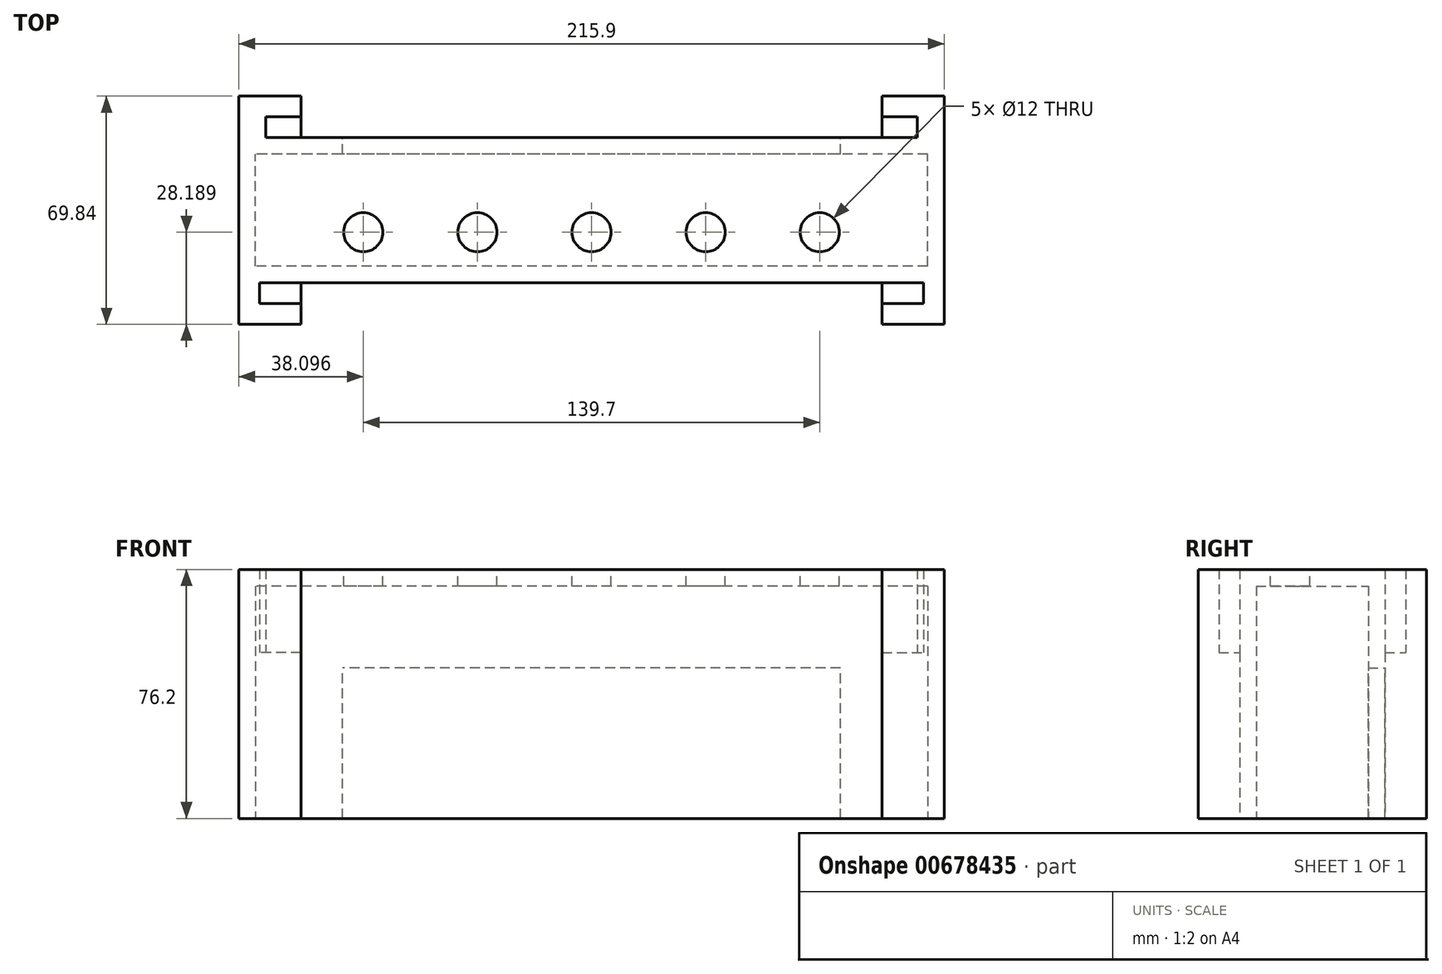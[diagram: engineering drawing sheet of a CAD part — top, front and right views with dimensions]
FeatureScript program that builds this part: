
annotation { "Feature Type Name" : "Feature", "Feature Type Description" : "" }
export const myFeature = defineFeature(function(context is Context, id is Id, definition is map)
    precondition{}
    {
        {
            var Q0;
            Q0=qCreatedBy(makeId("Top.planeOp"),FACE);
            var sketch = newSketch(context, id + "F0", { "sketchPlane" : qUnion([Q0])});
            skLineSegment(sketch, "E0.bottom", {"start": v(105.18, -22.23) * mm, "end": v(-110.72, -22.23) * mm});
            skLineSegment(sketch, "E0.top", {"start": v(105.18, 22.23) * mm, "end": v(-110.72, 22.22) * mm});
            skLineSegment(sketch, "E0.left", {"start": v(105.18, -22.23) * mm, "end": v(105.18, 22.22) * mm});
            skLineSegment(sketch, "E0.right", {"start": v(-110.72, -22.23) * mm, "end": v(-110.72, 22.22) * mm});
            skPoint(sketch, "E0.middle", {"position": v(-2.77, 0) * mm});
            skSolve(sketch);
        }
        {
            var Q0;
            Q0=makeQuery(id+"F0.imprint","IMPRINT",FACE,{"disambiguationData":[TD([[makeQuery(id+"F0.imprint","IMPRINT",EDGE,{"derivedFrom":sQuery(id+"F0.wireOp",EDGE,"E0.bottom")}),-1.0]])]});
            extrude(context, id + "F1", {"entities" : qUnion([Q0]), "depth" : 76.2 * mm, "offsetDistance" : 25.4 * mm});
        }
        {
            var Q0;
            Q0=makeQuery(id+"F1.opExtrude","CAP_FACE",FACE,{"disambiguationData":[OSD([sQuery(id+"F0.wireOp",EDGE,"E0.bottom"),sQuery(id+"F0.wireOp",EDGE,"E0.top"),sQuery(id+"F0.wireOp",EDGE,"E0.left"),sQuery(id+"F0.wireOp",EDGE,"E0.right")])],"isStart":true});
            shell(context, id + "F2", {"entities" : qUnion([Q0]), "thickness" : 5.08 * mm});
        }
        {
            var Q0;
            Q0=makeQuery(id+"F1.opExtrude","SWEPT_FACE",FACE,{"disambiguationData":[OSD([sQuery(id+"F0.wireOp",EDGE,"E0.bottom")])]});
            var sketch = newSketch(context, id + "F3", { "sketchPlane" : qUnion([Q0])});
            skLineSegment(sketch, "E1.bottom", {"start": v(-110.72, 76.2) * mm, "end": v(-104.37, 76.2) * mm});
            skLineSegment(sketch, "E1.top", {"start": v(-110.72, 0) * mm, "end": v(-104.37, 0) * mm});
            skLineSegment(sketch, "E1.left", {"start": v(-110.72, 76.2) * mm, "end": v(-110.72, 0) * mm});
            skLineSegment(sketch, "E1.right", {"start": v(-104.37, 76.2) * mm, "end": v(-104.37, 0) * mm});
            skLineSegment(sketch, "E2.bottom", {"start": v(105.18, 76.2) * mm, "end": v(98.83, 76.2) * mm});
            skLineSegment(sketch, "E2.top", {"start": v(105.18, 0) * mm, "end": v(98.83, 0) * mm});
            skLineSegment(sketch, "E2.left", {"start": v(105.18, 76.2) * mm, "end": v(105.18, 0) * mm});
            skLineSegment(sketch, "E2.right", {"start": v(98.83, 76.2) * mm, "end": v(98.83, 0) * mm});
            skSolve(sketch);
        }
        {
            var Q0;
            Q0=makeQuery(id+"F1.opExtrude","SWEPT_FACE",FACE,{"disambiguationData":[OSD([sQuery(id+"F0.wireOp",EDGE,"E0.top")])]});
            var sketch = newSketch(context, id + "F4", { "sketchPlane" : qUnion([Q0])});
            skLineSegment(sketch, "E3.bottom", {"start": v(-105.18, 76.2) * mm, "end": v(-98.83, 76.2) * mm});
            skLineSegment(sketch, "E3.top", {"start": v(-105.18, 0) * mm, "end": v(-98.83, 0) * mm});
            skLineSegment(sketch, "E3.left", {"start": v(-105.18, 76.2) * mm, "end": v(-105.18, 0) * mm});
            skLineSegment(sketch, "E3.right", {"start": v(-98.83, 76.2) * mm, "end": v(-98.83, 0) * mm});
            skLineSegment(sketch, "E4.bottom", {"start": v(110.72, 76.2) * mm, "end": v(104.37, 76.2) * mm});
            skLineSegment(sketch, "E4.top", {"start": v(110.72, 0) * mm, "end": v(104.37, 0) * mm});
            skLineSegment(sketch, "E4.left", {"start": v(110.72, 76.2) * mm, "end": v(110.72, 0) * mm});
            skLineSegment(sketch, "E4.right", {"start": v(104.37, 76.2) * mm, "end": v(104.37, 0) * mm});
            skSolve(sketch);
        }
        {
            var Q0;
            Q0=makeQuery(id+"F3.imprint","IMPRINT",FACE,{"disambiguationData":[TD([[makeQuery(id+"F3.imprint","IMPRINT",EDGE,{"derivedFrom":sQuery(id+"F3.wireOp",EDGE,"E1.bottom")}),1.0]])]});
            var Q1;
            Q1=makeQuery(id+"F3.imprint","IMPRINT",FACE,{"disambiguationData":[TD([[makeQuery(id+"F3.imprint","IMPRINT",EDGE,{"derivedFrom":sQuery(id+"F3.wireOp",EDGE,"E2.bottom")}),1.0]])]});
            extrude(context, id + "F5", {"entities" : qUnion([Q0, Q1]), "operationType" : NewBodyOperationType.ADD, "depth" : 12.7 * mm, "offsetDistance" : 25.4 * mm});
        }
        {
            var Q0;
            Q0=makeQuery(id+"F4.imprint","IMPRINT",FACE,{"disambiguationData":[TD([[makeQuery(id+"F4.imprint","IMPRINT",EDGE,{"derivedFrom":sQuery(id+"F4.wireOp",EDGE,"E3.bottom")}),-1.0]])]});
            var Q1;
            Q1=makeQuery(id+"F4.imprint","IMPRINT",FACE,{"disambiguationData":[TD([[makeQuery(id+"F4.imprint","IMPRINT",EDGE,{"derivedFrom":sQuery(id+"F4.wireOp",EDGE,"E4.bottom")}),-1.0]])]});
            extrude(context, id + "F6", {"entities" : qUnion([Q0, Q1]), "operationType" : NewBodyOperationType.ADD, "depth" : 12.7 * mm, "offsetDistance" : 25.4 * mm});
        }
        {
            var Q0;
            Q0=makeQuery(id+"FRrmfCGgLjqdVNs_1.boolean.opBoolean","MERGE",FACE,{"derivedFrom":[makeQuery(id+"FzGourxVZPiTFxx_1.boolean.opBoolean","MERGE",FACE,{"derivedFrom":[makeQuery(id+"F6.boolean.opBoolean","MERGE",FACE,{"derivedFrom":[makeQuery(id+"F5.boolean.opBoolean","MERGE",FACE,{"derivedFrom":[makeQuery(id+"F1.opExtrude","CAP_FACE",FACE,{"disambiguationData":[OSD([sQuery(id+"F0.wireOp",EDGE,"E0.bottom"),sQuery(id+"F0.wireOp",EDGE,"E0.top"),sQuery(id+"F0.wireOp",EDGE,"E0.left"),sQuery(id+"F0.wireOp",EDGE,"E0.right")])],"isStart":false}),makeQuery(id+"F5.opExtrude","SWEPT_FACE",FACE,{"disambiguationData":[OSD([sQuery(id+"F3.wireOp",EDGE,"E1.bottom")])]}),makeQuery(id+"F5.opExtrude","SWEPT_FACE",FACE,{"disambiguationData":[OSD([sQuery(id+"F3.wireOp",EDGE,"E2.bottom")])]})]}),makeQuery(id+"F6.opExtrude","SWEPT_FACE",FACE,{"disambiguationData":[OSD([sQuery(id+"F4.wireOp",EDGE,"E3.bottom")])]}),makeQuery(id+"F6.opExtrude","SWEPT_FACE",FACE,{"disambiguationData":[OSD([sQuery(id+"F4.wireOp",EDGE,"E4.bottom")])]})]}),makeQuery(id+"FzGourxVZPiTFxx_1.opExtrude","SWEPT_FACE",FACE,{"disambiguationData":[OSD([sQuery(id+"FrnQMVu3a4CgWtk_1.wireOp",EDGE,"r2tbibCh-ezkN-9FMi-7AQF-PA2gdZFEVCPD.bottom")])]}),makeQuery(id+"FzGourxVZPiTFxx_1.opExtrude","SWEPT_FACE",FACE,{"disambiguationData":[OSD([sQuery(id+"FhxCwb5BdVCvZEk_1.wireOp",EDGE,"8bSKoqo4-8QkT-eqxh-rGB9-fyDsR7UwIenD.bottom")])]})]}),makeQuery(id+"FRrmfCGgLjqdVNs_1.opExtrude","SWEPT_FACE",FACE,{"disambiguationData":[OSD([sQuery(id+"FhhxslobYrObnGy_1.wireOp",EDGE,"or8zbcxm-MRwS-TR7M-PYDy-Oy9PLmHRumrI.bottom")])]}),makeQuery(id+"FRrmfCGgLjqdVNs_1.opExtrude","SWEPT_FACE",FACE,{"disambiguationData":[OSD([sQuery(id+"FWsOcmM0LLO9Jgi_1.wireOp",EDGE,"o5xxpl94-z1vP-JHRe-kS0J-yNKfIfnKd3mt.bottom")])]})]});
            var sketch = newSketch(context, id + "F7", { "sketchPlane" : qUnion([Q0])});
            skCircle(sketch, "E5", {"center": v(67.08, -6.73) * mm, "radius": 6 * mm});
            skCircle(sketch, "E6", {"center": v(32.15, -6.73) * mm, "radius": 6 * mm});
            skCircle(sketch, "E7", {"center": v(-2.77, -6.73) * mm, "radius": 6 * mm});
            skCircle(sketch, "E8", {"center": v(-37.7, -6.73) * mm, "radius": 6 * mm});
            skCircle(sketch, "E9", {"center": v(-72.62, -6.73) * mm, "radius": 6 * mm});
            skSolve(sketch);
        }
        {
            var Q0;
            Q0=makeQuery(id+"F6.opExtrude","SWEPT_FACE",FACE,{"disambiguationData":[OSD([sQuery(id+"F4.wireOp",EDGE,"E3.right")])]});
            var sketch = newSketch(context, id + "F8", { "sketchPlane" : qUnion([Q0])});
            skLineSegment(sketch, "E10.bottom", {"start": v(-34.93, 76.2) * mm, "end": v(-28.58, 76.2) * mm});
            skLineSegment(sketch, "E10.top", {"start": v(-34.93, 0) * mm, "end": v(-28.58, 0) * mm});
            skLineSegment(sketch, "E10.left", {"start": v(-34.93, 76.2) * mm, "end": v(-34.93, 0) * mm});
            skLineSegment(sketch, "E10.right", {"start": v(-28.58, 76.2) * mm, "end": v(-28.58, 0) * mm});
            skLineSegment(sketch, "E11.bottom", {"start": v(-28.58, 0) * mm, "end": v(-22.23, 0) * mm});
            skLineSegment(sketch, "E11.top", {"start": v(-28.58, 50.8) * mm, "end": v(-22.23, 50.8) * mm});
            skLineSegment(sketch, "E11.left", {"start": v(-28.58, 0) * mm, "end": v(-28.58, 50.8) * mm});
            skLineSegment(sketch, "E11.right", {"start": v(-22.23, 0) * mm, "end": v(-22.23, 50.8) * mm});
            skSolve(sketch);
        }
        {
            var Q0;
            Q0=makeQuery(id+"F8.imprint","IMPRINT",FACE,{"disambiguationData":[TD([[makeQuery(id+"F8.imprint","IMPRINT",EDGE,{"derivedFrom":sQuery(id+"F8.wireOp",EDGE,"E10.bottom")}),-1.0]])]});
            var Q1;
            Q1=makeQuery(id+"F8.imprint","IMPRINT",FACE,{"disambiguationData":[TD([[makeQuery(id+"F8.imprint","IMPRINT",EDGE,{"derivedFrom":sQuery(id+"F8.wireOp",EDGE,"E11.bottom")}),1.0]])]});
            extrude(context, id + "F9", {"entities" : qUnion([Q0, Q1]), "operationType" : NewBodyOperationType.ADD, "depth" : 12.7 * mm, "offsetDistance" : 25.4 * mm});
        }
        {
            var Q0;
            Q0=makeQuery(id+"F6.opExtrude","SWEPT_FACE",FACE,{"disambiguationData":[OSD([sQuery(id+"F4.wireOp",EDGE,"E4.right")])]});
            var sketch = newSketch(context, id + "F10", { "sketchPlane" : qUnion([Q0])});
            skLineSegment(sketch, "E12.bottom", {"start": v(34.93, 76.2) * mm, "end": v(28.58, 76.2) * mm});
            skLineSegment(sketch, "E12.top", {"start": v(34.93, 0) * mm, "end": v(28.58, 0) * mm});
            skLineSegment(sketch, "E12.left", {"start": v(34.93, 76.2) * mm, "end": v(34.93, 0) * mm});
            skLineSegment(sketch, "E12.right", {"start": v(28.58, 76.2) * mm, "end": v(28.58, 0) * mm});
            skLineSegment(sketch, "E13.bottom", {"start": v(28.58, 0) * mm, "end": v(22.23, 0) * mm});
            skLineSegment(sketch, "E13.top", {"start": v(28.58, 50.8) * mm, "end": v(22.23, 50.8) * mm});
            skLineSegment(sketch, "E13.left", {"start": v(28.58, 0) * mm, "end": v(28.58, 50.8) * mm});
            skLineSegment(sketch, "E13.right", {"start": v(22.23, 0) * mm, "end": v(22.23, 50.8) * mm});
            skSolve(sketch);
        }
        {
            var Q0;
            Q0=makeQuery(id+"F10.imprint","IMPRINT",FACE,{"disambiguationData":[TD([[makeQuery(id+"F10.imprint","IMPRINT",EDGE,{"derivedFrom":sQuery(id+"F10.wireOp",EDGE,"E12.bottom")}),1.0]])]});
            var Q1;
            Q1=makeQuery(id+"F10.imprint","IMPRINT",FACE,{"disambiguationData":[TD([[makeQuery(id+"F10.imprint","IMPRINT",EDGE,{"derivedFrom":sQuery(id+"F10.wireOp",EDGE,"E13.bottom")}),-1.0]])]});
            extrude(context, id + "F11", {"entities" : qUnion([Q0, Q1]), "operationType" : NewBodyOperationType.ADD, "depth" : 12.7 * mm, "offsetDistance" : 25.4 * mm});
        }
        {
            var Q0;
            Q0=makeQuery(id+"F5.opExtrude","SWEPT_FACE",FACE,{"disambiguationData":[OSD([sQuery(id+"F3.wireOp",EDGE,"E1.right")])]});
            var sketch = newSketch(context, id + "F12", { "sketchPlane" : qUnion([Q0])});
            skLineSegment(sketch, "E14.bottom", {"start": v(-34.93, 0) * mm, "end": v(-28.58, 0) * mm});
            skLineSegment(sketch, "E14.top", {"start": v(-34.93, 76.2) * mm, "end": v(-28.58, 76.2) * mm});
            skLineSegment(sketch, "E14.left", {"start": v(-34.93, 0) * mm, "end": v(-34.93, 76.2) * mm});
            skLineSegment(sketch, "E14.right", {"start": v(-28.58, 0) * mm, "end": v(-28.58, 76.2) * mm});
            skLineSegment(sketch, "E15.bottom", {"start": v(-28.58, 0) * mm, "end": v(-22.23, 0) * mm});
            skLineSegment(sketch, "E15.top", {"start": v(-28.58, 50.8) * mm, "end": v(-22.23, 50.8) * mm});
            skLineSegment(sketch, "E15.left", {"start": v(-28.58, 0) * mm, "end": v(-28.58, 50.8) * mm});
            skLineSegment(sketch, "E15.right", {"start": v(-22.23, 0) * mm, "end": v(-22.23, 50.8) * mm});
            skSolve(sketch);
        }
        {
            var Q0;
            Q0=makeQuery(id+"F12.imprint","IMPRINT",FACE,{"disambiguationData":[TD([[makeQuery(id+"F12.imprint","IMPRINT",EDGE,{"derivedFrom":sQuery(id+"F12.wireOp",EDGE,"E14.bottom")}),1.0]])]});
            var Q1;
            Q1=makeQuery(id+"F12.imprint","IMPRINT",FACE,{"disambiguationData":[TD([[makeQuery(id+"F12.imprint","IMPRINT",EDGE,{"derivedFrom":sQuery(id+"F12.wireOp",EDGE,"E15.bottom")}),1.0]])]});
            extrude(context, id + "F13", {"entities" : qUnion([Q0, Q1]), "operationType" : NewBodyOperationType.ADD, "depth" : 12.7 * mm, "offsetDistance" : 25.4 * mm});
        }
        {
            var Q0;
            Q0=makeQuery(id+"F5.opExtrude","SWEPT_FACE",FACE,{"disambiguationData":[OSD([sQuery(id+"F3.wireOp",EDGE,"E2.right")])]});
            var sketch = newSketch(context, id + "F14", { "sketchPlane" : qUnion([Q0])});
            skLineSegment(sketch, "E16.bottom", {"start": v(34.93, 76.2) * mm, "end": v(28.58, 76.2) * mm});
            skLineSegment(sketch, "E16.top", {"start": v(34.93, 0) * mm, "end": v(28.58, 0) * mm});
            skLineSegment(sketch, "E16.left", {"start": v(34.93, 76.2) * mm, "end": v(34.93, 0) * mm});
            skLineSegment(sketch, "E16.right", {"start": v(28.58, 76.2) * mm, "end": v(28.58, 0) * mm});
            skLineSegment(sketch, "E17.bottom", {"start": v(28.58, 0) * mm, "end": v(22.23, 0) * mm});
            skLineSegment(sketch, "E17.top", {"start": v(28.58, 50.8) * mm, "end": v(22.23, 50.8) * mm});
            skLineSegment(sketch, "E17.left", {"start": v(28.58, 0) * mm, "end": v(28.58, 50.8) * mm});
            skLineSegment(sketch, "E17.right", {"start": v(22.23, 0) * mm, "end": v(22.23, 50.8) * mm});
            skSolve(sketch);
        }
        {
            var Q0;
            Q0=makeQuery(id+"F14.imprint","IMPRINT",FACE,{"disambiguationData":[TD([[makeQuery(id+"F14.imprint","IMPRINT",EDGE,{"derivedFrom":sQuery(id+"F14.wireOp",EDGE,"E16.bottom")}),1.0]])]});
            var Q1;
            Q1=makeQuery(id+"F14.imprint","IMPRINT",FACE,{"disambiguationData":[TD([[makeQuery(id+"F14.imprint","IMPRINT",EDGE,{"derivedFrom":sQuery(id+"F14.wireOp",EDGE,"E17.bottom")}),-1.0]])]});
            extrude(context, id + "F15", {"entities" : qUnion([Q0, Q1]), "operationType" : NewBodyOperationType.ADD, "depth" : 12.7 * mm, "offsetDistance" : 25.4 * mm});
        }
        {
            var Q0;
            Q0=makeQuery(id+"F1.opExtrude","SWEPT_FACE",FACE,{"disambiguationData":[OSD([sQuery(id+"F0.wireOp",EDGE,"E0.top")])]});
            var sketch = newSketch(context, id + "F16", { "sketchPlane" : qUnion([Q0])});
            skLineSegment(sketch, "E18.bottom", {"start": v(-73.43, 0) * mm, "end": v(78.97, 0) * mm});
            skLineSegment(sketch, "E18.top", {"start": v(-73.43, 46.08) * mm, "end": v(78.97, 46.08) * mm});
            skLineSegment(sketch, "E18.left", {"start": v(-73.43, 0) * mm, "end": v(-73.43, 46.08) * mm});
            skLineSegment(sketch, "E18.right", {"start": v(78.97, 0) * mm, "end": v(78.97, 46.08) * mm});
            skSolve(sketch);
        }
        {
            var Q0;
            Q0=makeQuery(id+"F16.imprint","IMPRINT",FACE,{"disambiguationData":[TD([[makeQuery(id+"F16.imprint","IMPRINT",EDGE,{"derivedFrom":sQuery(id+"F16.wireOp",EDGE,"E18.bottom")}),1.0]])]});
            extrude(context, id + "F17", {"entities" : qUnion([Q0]), "operationType" : NewBodyOperationType.REMOVE, "oppositeDirection" : true, "depth" : 5.08 * mm, "offsetDistance" : 25.4 * mm});
        }
        {
            var Q0;
            Q0=makeQuery(id+"F7.imprint","IMPRINT",FACE,{"disambiguationData":[TD([[makeQuery(id+"F7.imprint","IMPRINT",EDGE,{"derivedFrom":sQuery(id+"F7.wireOp",EDGE,"E5")}),1.0]])]});
            var Q1;
            Q1=makeQuery(id+"F7.imprint","IMPRINT",FACE,{"disambiguationData":[TD([[makeQuery(id+"F7.imprint","IMPRINT",EDGE,{"derivedFrom":sQuery(id+"F7.wireOp",EDGE,"E6")}),1.0]])]});
            var Q2;
            Q2=makeQuery(id+"F7.imprint","IMPRINT",FACE,{"disambiguationData":[TD([[makeQuery(id+"F7.imprint","IMPRINT",EDGE,{"derivedFrom":sQuery(id+"F7.wireOp",EDGE,"E7")}),1.0]])]});
            var Q3;
            Q3=makeQuery(id+"F7.imprint","IMPRINT",FACE,{"disambiguationData":[TD([[makeQuery(id+"F7.imprint","IMPRINT",EDGE,{"derivedFrom":sQuery(id+"F7.wireOp",EDGE,"E8")}),1.0]])]});
            var Q4;
            Q4=makeQuery(id+"F7.imprint","IMPRINT",FACE,{"disambiguationData":[TD([[makeQuery(id+"F7.imprint","IMPRINT",EDGE,{"derivedFrom":sQuery(id+"F7.wireOp",EDGE,"E9")}),1.0]])]});
            extrude(context, id + "F18", {"entities" : qUnion([Q0, Q1, Q2, Q3, Q4]), "operationType" : NewBodyOperationType.REMOVE, "oppositeDirection" : true, "depth" : 5.08 * mm, "offsetDistance" : 25.4 * mm});
        }
        {
            var Q0;
            Q0=makeQuery(id+"F9.opExtrude","SWEPT_FACE",FACE,{"disambiguationData":[OSD([sQuery(id+"F8.wireOp",EDGE,"E11.top")])]});
            var sketch = newSketch(context, id + "F19", { "sketchPlane" : qUnion([Q0])});
            skLineSegment(sketch, "E19.bottom", {"start": v(98.83, 22.23) * mm, "end": v(96.92, 22.23) * mm});
            skLineSegment(sketch, "E19.top", {"start": v(98.83, 28.58) * mm, "end": v(96.92, 28.58) * mm});
            skLineSegment(sketch, "E19.left", {"start": v(98.83, 22.23) * mm, "end": v(98.83, 28.58) * mm});
            skLineSegment(sketch, "E19.right", {"start": v(96.92, 22.23) * mm, "end": v(96.92, 28.58) * mm});
            skSolve(sketch);
        }
        {
            var Q0;
            Q0=makeQuery(id+"F11.opExtrude","SWEPT_FACE",FACE,{"disambiguationData":[OSD([sQuery(id+"F10.wireOp",EDGE,"E13.top")])]});
            var sketch = newSketch(context, id + "F20", { "sketchPlane" : qUnion([Q0])});
            skLineSegment(sketch, "E20.bottom", {"start": v(-104.37, 22.22) * mm, "end": v(-102.47, 22.22) * mm});
            skLineSegment(sketch, "E20.top", {"start": v(-104.37, 28.57) * mm, "end": v(-102.47, 28.57) * mm});
            skLineSegment(sketch, "E20.left", {"start": v(-104.37, 22.22) * mm, "end": v(-104.37, 28.57) * mm});
            skLineSegment(sketch, "E20.right", {"start": v(-102.47, 22.22) * mm, "end": v(-102.47, 28.57) * mm});
            skSolve(sketch);
        }
        {
            var Q0;
            Q0=makeQuery(id+"F20.imprint","IMPRINT",FACE,{"disambiguationData":[TD([[makeQuery(id+"F20.imprint","IMPRINT",EDGE,{"derivedFrom":sQuery(id+"F20.wireOp",EDGE,"E20.bottom")}),-1.0]])]});
            var Q1;
            Q1=makeQuery(id+"F19.imprint","IMPRINT",FACE,{"disambiguationData":[TD([[makeQuery(id+"F19.imprint","IMPRINT",EDGE,{"derivedFrom":sQuery(id+"F19.wireOp",EDGE,"E19.bottom")}),1.0]])]});
            extrude(context, id + "F21", {"entities" : qUnion([Q0, Q1]), "operationType" : NewBodyOperationType.ADD, "depth" : 25.4 * mm, "offsetDistance" : 25.4 * mm});
        }
    });
